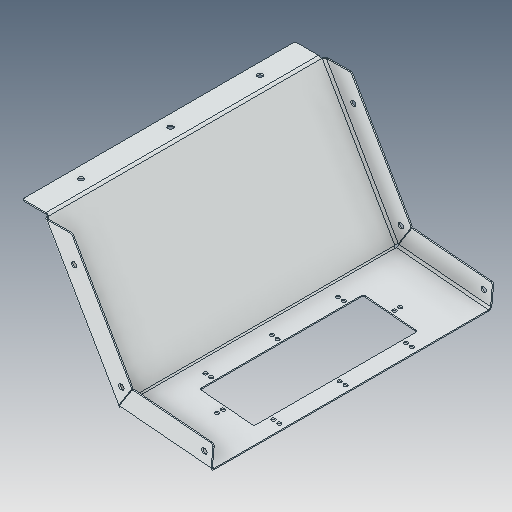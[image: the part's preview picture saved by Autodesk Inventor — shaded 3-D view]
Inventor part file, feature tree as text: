
AUTODESK INVENTOR PART (.ipt)
format: ipt  version: 2023.5 (Build 275446000, 446)  size: 215,040 bytes
history: native  units: in
note: dims shown in document units (in); Inventor stores cm internally (conversion verified against a paired STEP export)
features: fillet x1
ambient origin geometry x8: Origin, YZ Plane, XZ Plane, XY Plane, X Axis, Y Axis, Z Axis, Center Point
bodies: Solid1 (feature_tree)
feature tree (1):
  fillet  "Fillet5"  [1 undecoded]
note: 1 required parameter value undecoded (feature->parameter linkage not recoverable at this tier; creation-order binding heuristic only, values carry confidence <= 0.55)
